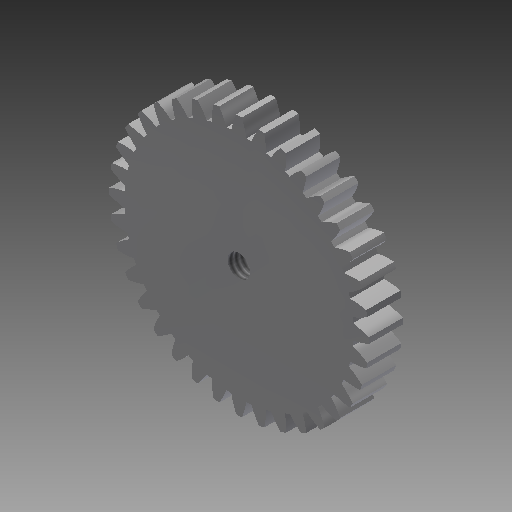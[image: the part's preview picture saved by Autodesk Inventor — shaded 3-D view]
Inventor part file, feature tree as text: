
AUTODESK INVENTOR PART (.ipt)
format: ipt  version: 2017 (Build 210142000, 142)  size: 289,792 bytes
history: native  units: mm (DEFAULTED — no unit token found)
features: plane x3, other x3, sketch x3, extrude x1, hole x1
ambient origin geometry x8: Origin, YZ Plane, XZ Plane, XY Plane, X Axis, Y Axis, Z Axis, Center Point
bodies: Solid1 (feature_tree)
feature tree (11):
  extrude  "Extrusion1"  Depth=5.0mm TaperAngle=0.0deg
  plane  "Work Plane2"
  plane  "Work Plane8"
  plane  "Work Plane9"
  other  "Spur Gear"
  hole  "Hole1"  [1 undecoded]
  sketch  "Sketch1"  dims[d0=38.0mm d1=5.0mm d2=0.0mm]
  sketch  "Sketch2"  dims[d3=36.0mm d4=10.0mm d5=0.0mm]
  other  "Srf1"
  sketch  "Sketch3"  dims[d16=36.0mm d17=0.0mm d34=0.872665mm d39=0.0mm d41=0.0mm d43=36.0mm d46=36.0mm d47=0.0mm d48=0.0mm d49=3.302mm d50=8.331mm d51=4.0mm d52=2.0mm d53=90.0deg d54=12.3mm d55=20.594885mm]
  other  "Pitch Diameter"
note: 1 required parameter value undecoded (feature->parameter linkage not recoverable at this tier; creation-order binding heuristic only, values carry confidence <= 0.55)
